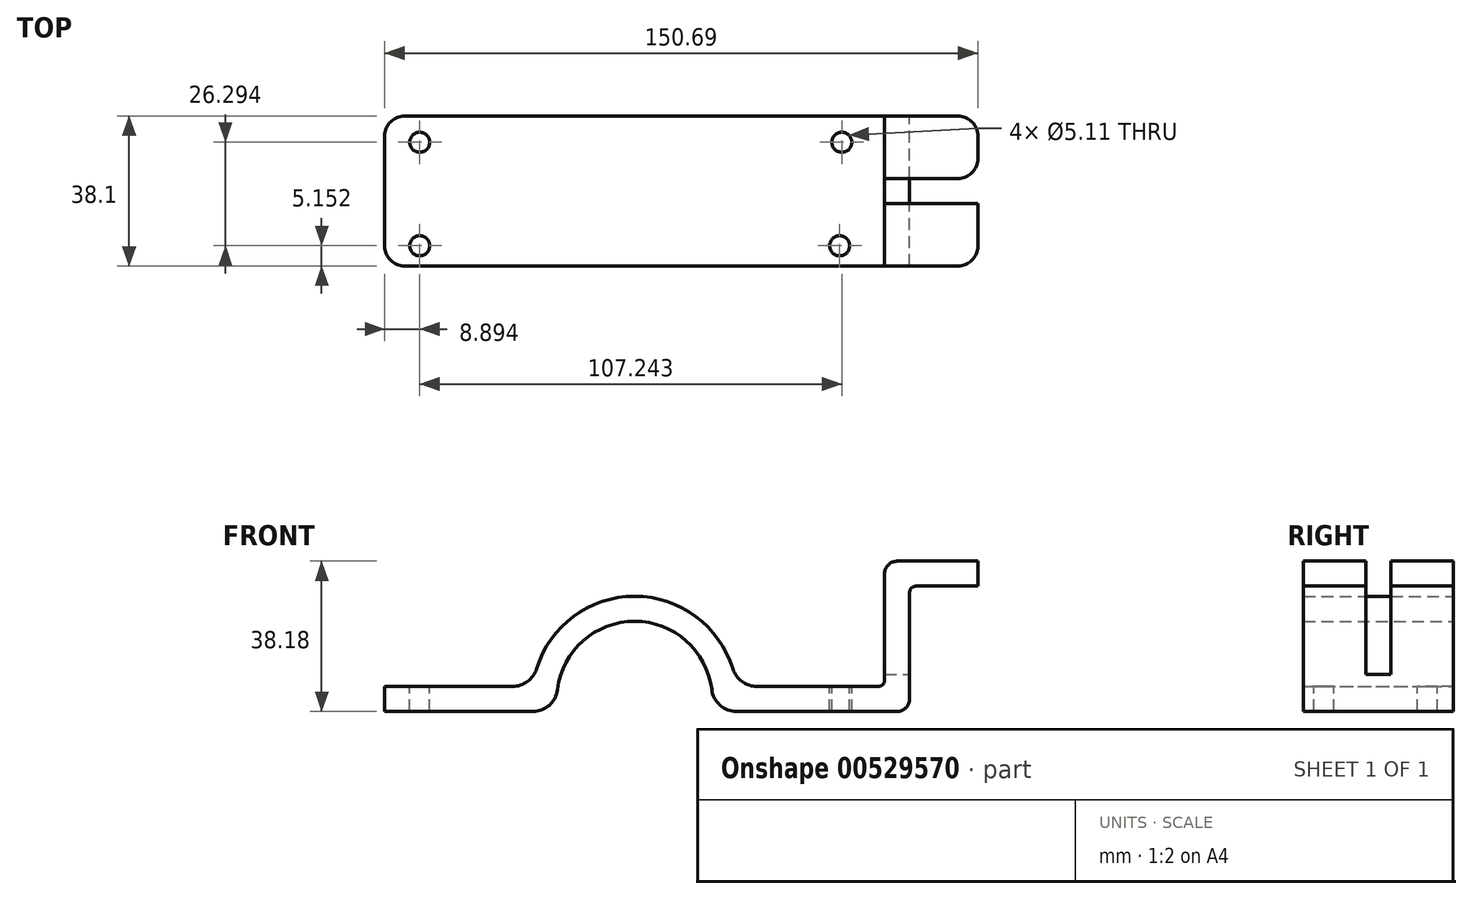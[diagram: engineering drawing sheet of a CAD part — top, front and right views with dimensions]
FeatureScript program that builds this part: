
annotation { "Feature Type Name" : "Feature", "Feature Type Description" : "" }
export const myFeature = defineFeature(function(context is Context, id is Id, definition is map)
    precondition{}
    {
        {
            var Q0;
            Q0=qCreatedBy(makeId("Front.planeOp"),FACE);
            var sketch = newSketch(context, id + "F0", { "sketchPlane" : qUnion([Q0])});
            skLineSegment(sketch, "E0.bottom", {"start": v(-63.5, -3.18) * mm, "end": v(-25.9, -3.18) * mm});
            skLineSegment(sketch, "E0.top", {"start": v(-63.5, 3.18) * mm, "end": v(-31, 3.18) * mm});
            skLineSegment(sketch, "E0.left", {"start": v(-63.5, -3.18) * mm, "end": v(-63.5, 3.18) * mm});
            skPoint(sketch, "E0.middle", {"position": v(0, 0) * mm});
            skArc(sketch, "E1", {"start": v(24.93, 7.66) * mm, "mid": v(0, 26.08) * mm, "end": v(-24.93, 7.66) * mm});
            skArc(sketch, "E2.0", {"start": v(19.59, 2.4) * mm, "mid": v(0, 19.73) * mm, "end": v(-19.59, 2.4) * mm});
            skLineSegment(sketch, "E3.trimOffspring", {"start": v(31, 3.18) * mm, "end": v(61.91, 3.18) * mm});
            skLineSegment(sketch, "E4.trimOffspring", {"start": v(25.9, -3.18) * mm, "end": v(63.5, -3.18) * mm});
            skLineSegment(sketch, "E5.bottom", {"start": v(63.5, -3.18) * mm, "end": v(66.67, -3.18) * mm});
            skLineSegment(sketch, "E5.left", {"start": v(63.5, 4.76) * mm, "end": v(63.5, 31.83) * mm});
            skLineSegment(sketch, "E5.right", {"start": v(69.85, 0) * mm, "end": v(69.85, 27.06) * mm});
            skLineSegment(sketch, "E6.bottom", {"start": v(66.67, 35) * mm, "end": v(87.2, 35) * mm});
            skLineSegment(sketch, "E6.top", {"start": v(71.44, 28.65) * mm, "end": v(87.2, 28.65) * mm});
            skLineSegment(sketch, "E6.right", {"start": v(87.2, 35) * mm, "end": v(87.2, 28.65) * mm});
            skPoint(sketch, "E7.visualSharp", {"position": v(69.85, -3.18) * mm});
            skArc(sketch, "E7.filletArc", {"start": v(66.67, -3.18) * mm, "mid": v(68.92, -2.25) * mm, "end": v(69.85, 0) * mm});
            skPoint(sketch, "E8.visualSharp", {"position": v(63.5, 3.18) * mm});
            skArc(sketch, "E8.filletArc", {"start": v(61.91, 3.18) * mm, "mid": v(63.04, 3.64) * mm, "end": v(63.5, 4.76) * mm});
            skPoint(sketch, "E9.visualSharp", {"position": v(69.85, 28.65) * mm});
            skArc(sketch, "E9.filletArc", {"start": v(71.44, 28.65) * mm, "mid": v(70.31, 28.19) * mm, "end": v(69.85, 27.06) * mm});
            skPoint(sketch, "E10.visualSharp", {"position": v(63.5, 35) * mm});
            skArc(sketch, "E10.filletArc", {"start": v(66.67, 35) * mm, "mid": v(64.43, 34.07) * mm, "end": v(63.5, 31.83) * mm});
            skPoint(sketch, "E11.visualSharp", {"position": v(-25.9, 3.18) * mm});
            skArc(sketch, "E11.filletArc", {"start": v(-31, 3.18) * mm, "mid": v(-27.23, 4.42) * mm, "end": v(-24.93, 7.66) * mm});
            skPoint(sketch, "E12.visualSharp", {"position": v(25.9, 3.18) * mm});
            skArc(sketch, "E12.filletArc", {"start": v(24.93, 7.66) * mm, "mid": v(27.23, 4.42) * mm, "end": v(31, 3.18) * mm});
            skPoint(sketch, "E13.visualSharp", {"position": v(19.48, -3.18) * mm});
            skArc(sketch, "E13.filletArc", {"start": v(19.59, 2.4) * mm, "mid": v(21.68, -1.58) * mm, "end": v(25.9, -3.18) * mm});
            skPoint(sketch, "E14.visualSharp", {"position": v(-19.48, -3.18) * mm});
            skArc(sketch, "E14.filletArc", {"start": v(-25.9, -3.18) * mm, "mid": v(-21.68, -1.58) * mm, "end": v(-19.59, 2.4) * mm});
            skSolve(sketch);
        }
        {
            var Q0;
            Q0 = qSketchRegion(id + "F0", true);
            extrude(context, id + "F1", {"entities" : qUnion([Q0]), "endBound" : BoundingType.SYMMETRIC, "depth" : 38.1 * mm, "offsetDistance" : 25.4 * mm});
        }
        {
            var Q0;
            Q0=makeQuery(id+"F1.opExtrude","SWEPT_FACE",FACE,{"disambiguationData":[OSD([sQuery(id+"F0.wireOp",EDGE,"E6.right")])]});
            var sketch = newSketch(context, id + "F2", { "sketchPlane" : qUnion([Q0])});
            skLineSegment(sketch, "E15.right", {"start": v(-3.18, 35) * mm, "end": v(-3.18, 6.2) * mm});
            skLineSegment(sketch, "E16.right", {"start": v(3.17, 6.2) * mm, "end": v(3.17, 35) * mm});
            skLineSegment(sketch, "E17.0", {"start": v(6.35, 6.2) * mm, "end": v(6.35, 35) * mm});
            skPoint(sketch, "E15.left.start.orphan", {"position": v(0, 35) * mm});
            skLineSegment(sketch, "E18", {"start": v(-3.18, 6.2) * mm, "end": v(3.17, 6.2) * mm});
            skLineSegment(sketch, "E19", {"start": v(3.17, 35) * mm, "end": v(-3.18, 35) * mm});
            skSolve(sketch);
        }
        {
            var Q0;
            Q0 = qSketchRegion(id + "F2", true);
            extrude(context, id + "F3", {"entities" : qUnion([Q0]), "operationType" : NewBodyOperationType.REMOVE, "oppositeDirection" : true, "depth" : 25.4 * mm, "offsetDistance" : 25.4 * mm});
        }
        {
            var Q0;
            Q0=makeQuery(id+"F1.opExtrude","CAP_EDGE",EDGE,{"disambiguationData":[OSD([sQuery(id+"F0.wireOp",EDGE,"E0.left")])],"isStart":false});
            var Q1;
            Q1=makeQuery(id+"F1.opExtrude","CAP_EDGE",EDGE,{"disambiguationData":[OSD([sQuery(id+"F0.wireOp",EDGE,"E0.left")])],"isStart":true});
            var Q2;
            Q2=makeQuery(id+"F1.opExtrude","CAP_EDGE",EDGE,{"disambiguationData":[OSD([sQuery(id+"F0.wireOp",EDGE,"E6.right")])],"isStart":true});
            var Q3;
            Q3=makeQuery(id+"F3.boolean.opBoolean","COPY",EDGE,{"derivedFrom":makeQuery(id+"F3.opExtrude","CAP_EDGE",EDGE,{"disambiguationData":[OSD([sQuery(id+"F2.wireOp",EDGE,"E16.right")])],"isStart":true})});
            var Q4;
            Q4=makeQuery(id+"F3.boolean.opBoolean","COPY",EDGE,{"derivedFrom":makeQuery(id+"F3.opExtrude","CAP_EDGE",EDGE,{"disambiguationData":[OSD([sQuery(id+"F2.wireOp",EDGE,"E15.right")])],"isStart":true})});
            var Q5;
            Q5=makeQuery(id+"F1.opExtrude","CAP_EDGE",EDGE,{"disambiguationData":[OSD([sQuery(id+"F0.wireOp",EDGE,"E6.right")])],"isStart":false});
            fillet(context, id + "F4", {"entities" : qUnion([Q0, Q1, Q2, Q3, Q4, Q5]), "radius" : 5.08 * mm, "tangentPropagation" : true, "allowEdgeOverflow" : false});
        }
        {
            var Q0;
            Q0=makeQuery(id+"F1.opExtrude","SWEPT_FACE",FACE,{"disambiguationData":[OSD([sQuery(id+"F0.wireOp",EDGE,"E0.top")])]});
            var sketch = newSketch(context, id + "F5", { "sketchPlane" : qUnion([Q0])});
            skPoint(sketch, "E20", {"position": v(-54.6, 12.4) * mm});
            skPoint(sketch, "E21", {"position": v(-54.6, -13.9) * mm});
            skPoint(sketch, "E22", {"position": v(52.07, -13.9) * mm});
            skPoint(sketch, "E23", {"position": v(52.64, 12.4) * mm});
            skSolve(sketch);
        }
        {
            var Q0;
            Q0=sQuery(id+"F5.wireOp",VERTEX,"E20");
            var Q1;
            Q1=sQuery(id+"F5.wireOp",VERTEX,"E21");
            var Q2;
            Q2=sQuery(id+"F5.wireOp",VERTEX,"a4ac427e-0513-4d14-b022-bf81b28b5892");
            var Q3;
            Q3=sQuery(id+"F5.wireOp",VERTEX,"E23");
            var Q4;
            Q4=sQuery(id+"F5.wireOp",VERTEX,"E22");
            var Q5;
            Q5=makeQuery(id+"F1.opExtrude","SWEPT_BODY",BODY,{"disambiguationData":[OSD([sQuery(id+"F0.wireOp",EDGE,"E0.bottom"),sQuery(id+"F0.wireOp",EDGE,"E0.top"),sQuery(id+"F0.wireOp",EDGE,"E0.left"),sQuery(id+"F0.wireOp",EDGE,"E1"),sQuery(id+"F0.wireOp",EDGE,"E2.0"),sQuery(id+"F0.wireOp",EDGE,"E3.trimOffspring"),sQuery(id+"F0.wireOp",EDGE,"E4.trimOffspring"),sQuery(id+"F0.wireOp",EDGE,"E5.bottom"),sQuery(id+"F0.wireOp",EDGE,"E5.left"),sQuery(id+"F0.wireOp",EDGE,"E5.right"),sQuery(id+"F0.wireOp",EDGE,"E6.bottom"),sQuery(id+"F0.wireOp",EDGE,"E6.top"),sQuery(id+"F0.wireOp",EDGE,"E6.right"),sQuery(id+"F0.wireOp",EDGE,"E7.filletArc"),sQuery(id+"F0.wireOp",EDGE,"E8.filletArc"),sQuery(id+"F0.wireOp",EDGE,"E9.filletArc"),sQuery(id+"F0.wireOp",EDGE,"E10.filletArc"),sQuery(id+"F0.wireOp",EDGE,"E11.filletArc"),sQuery(id+"F0.wireOp",EDGE,"E12.filletArc"),sQuery(id+"F0.wireOp",EDGE,"E13.filletArc"),sQuery(id+"F0.wireOp",EDGE,"E14.filletArc")])]});
            hole(context, id + "F6", {"style" : HoleStyle.SIMPLE, "endStyle" : HoleEndStyle.THROUGH, "standardTappedOrClearance" : lookupTablePath({ "standard" : "ANSI", "engagement" : "75%", "pitch" : "20 tpi", "size" : "1/4", "type" : "Tapped" }), "standardBlindInLast" : lookupTablePath({ "standard" : "ANSI", "engagement" : "75%", "pitch" : "20 tpi", "size" : "1/4", "type" : "Tapped" }), "holeDiameter" : 5.1 * mm, "showTappedDepth" : true, "isTappedThrough" : true, "tappedDepth" : 12.7 * mm, "tapClearance" : 3, "locations" : qUnion([Q0, Q1, Q2, Q3, Q4]), "scope" : qUnion([Q5]), "majorDiameter" : 6.35 * mm});
        }
    });
